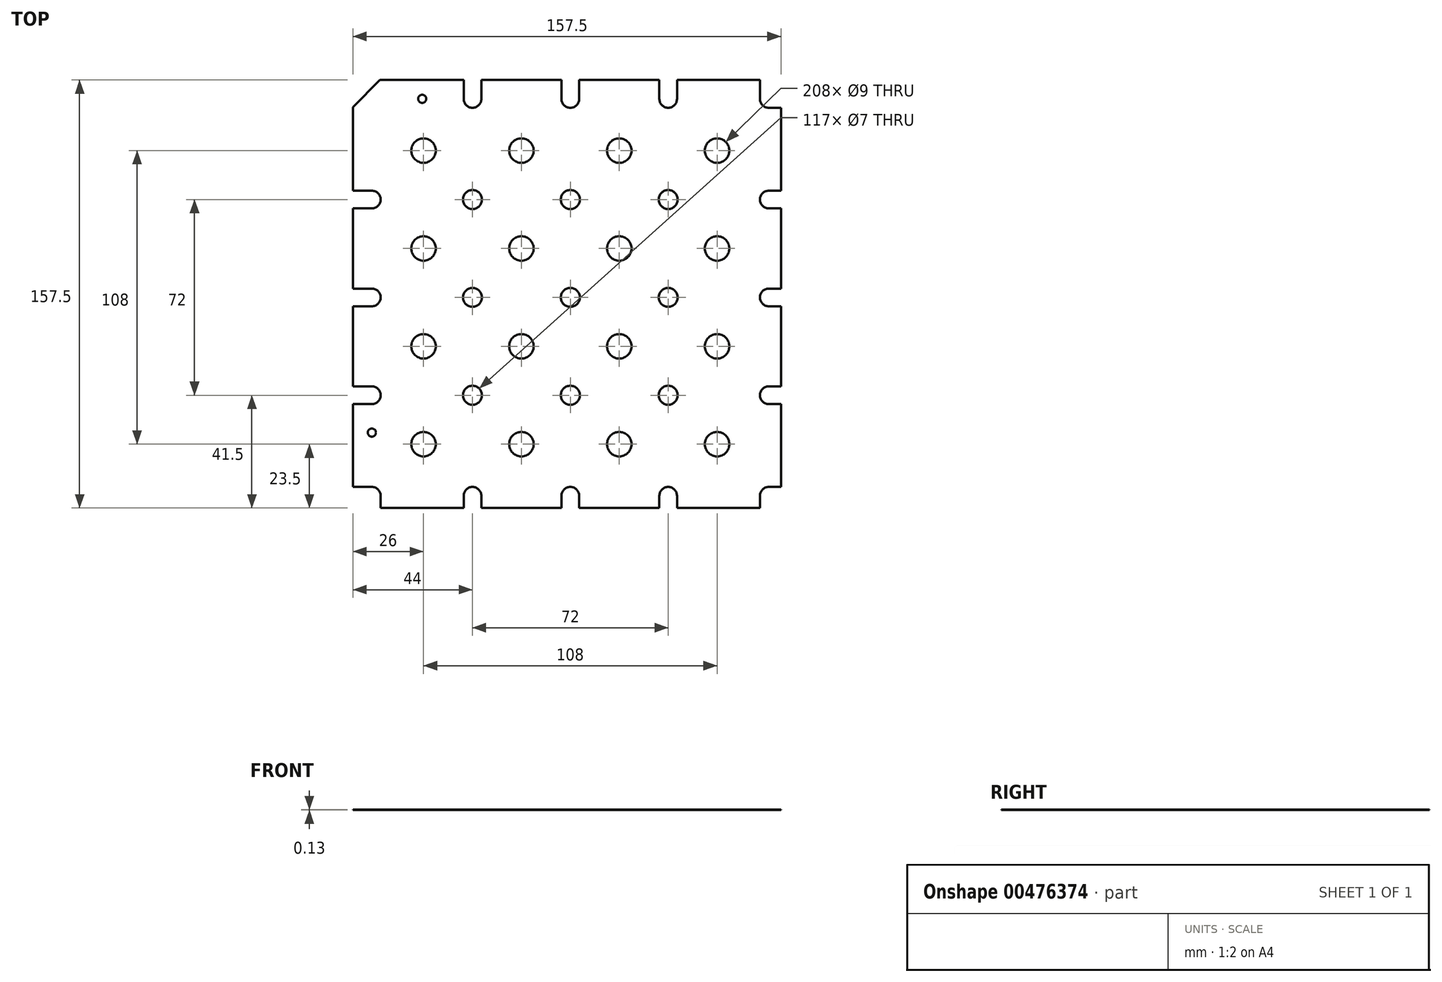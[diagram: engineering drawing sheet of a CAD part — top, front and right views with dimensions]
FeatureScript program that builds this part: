
annotation { "Feature Type Name" : "Feature", "Feature Type Description" : "" }
export const myFeature = defineFeature(function(context is Context, id is Id, definition is map)
    precondition{}
    {
        {
            var Q0;
            Q0=qCreatedBy(makeId("Top.planeOp"),FACE);
            var sketch = newSketch(context, id + "F0", { "sketchPlane" : qUnion([Q0])});
            skCircle(sketch, "E0", {"center": v(0, 0) * mm, "radius": 1.5 * mm});
            skCircle(sketch, "E1", {"center": v(18.5, 122.8) * mm, "radius": 1.5 * mm});
            skLineSegment(sketch, "E2.bottom", {"start": v(142.75, 129.75) * mm, "end": v(112.25, 129.75) * mm});
            skLineSegment(sketch, "E2.top", {"start": v(142.75, -27.75) * mm, "end": v(112.25, -27.75) * mm});
            skLineSegment(sketch, "E2.left", {"start": v(150.5, 119.5) * mm, "end": v(150.5, 89) * mm});
            skLineSegment(sketch, "E2.right", {"start": v(-7, 119.75) * mm, "end": v(-7, 89) * mm});
            skCircle(sketch, "E3", {"center": v(19, -4.25) * mm, "radius": 4.5 * mm});
            skCircle(sketch, "E4.0.1.0", {"center": v(19, 31.75) * mm, "radius": 4.5 * mm});
            skCircle(sketch, "E4.0.2.0", {"center": v(19, 67.75) * mm, "radius": 4.5 * mm});
            skCircle(sketch, "E4.0.3.0", {"center": v(19, 103.75) * mm, "radius": 4.5 * mm});
            skCircle(sketch, "E4.1.0.0", {"center": v(55, -4.25) * mm, "radius": 4.5 * mm});
            skCircle(sketch, "E4.1.1.0", {"center": v(55, 31.75) * mm, "radius": 4.5 * mm});
            skCircle(sketch, "E4.1.2.0", {"center": v(55, 67.75) * mm, "radius": 4.5 * mm});
            skCircle(sketch, "E4.1.3.0", {"center": v(55, 103.75) * mm, "radius": 4.5 * mm});
            skCircle(sketch, "E4.2.0.0", {"center": v(91, -4.25) * mm, "radius": 4.5 * mm});
            skCircle(sketch, "E4.2.1.0", {"center": v(91, 31.75) * mm, "radius": 4.5 * mm});
            skCircle(sketch, "E4.2.2.0", {"center": v(91, 67.75) * mm, "radius": 4.5 * mm});
            skCircle(sketch, "E4.2.3.0", {"center": v(91, 103.75) * mm, "radius": 4.5 * mm});
            skCircle(sketch, "E4.3.0.0", {"center": v(127, -4.25) * mm, "radius": 4.5 * mm});
            skCircle(sketch, "E4.3.1.0", {"center": v(127, 31.75) * mm, "radius": 4.5 * mm});
            skCircle(sketch, "E4.3.2.0", {"center": v(127, 67.75) * mm, "radius": 4.5 * mm});
            skCircle(sketch, "E4.3.3.0", {"center": v(127, 103.75) * mm, "radius": 4.5 * mm});
            skLineSegment(sketch, "E4.direction1", {"start": v(19, -4.25) * mm, "end": v(55, -4.25) * mm, "construction": true});
            skLineSegment(sketch, "E4.direction2", {"start": v(19, -4.25) * mm, "end": v(19, 31.75) * mm, "construction": true});
            skLineSegment(sketch, "E5", {"start": v(33.75, -23.25) * mm, "end": v(33.75, -27.75) * mm});
            skLineSegment(sketch, "E6", {"start": v(40.25, -23.25) * mm, "end": v(40.25, -27.75) * mm});
            skArc(sketch, "E7", {"start": v(33.75, -23.25) * mm, "mid": v(37, -20) * mm, "end": v(40.25, -23.25) * mm});
            skLineSegment(sketch, "E8.trimOffspring", {"start": v(33.75, -27.75) * mm, "end": v(3.25, -27.75) * mm});
            skLineSegment(sketch, "E9.1.0.0", {"start": v(69.75, -23.25) * mm, "end": v(69.75, -27.75) * mm});
            skArc(sketch, "E9.1.0.1", {"start": v(69.75, -23.25) * mm, "mid": v(73, -20) * mm, "end": v(76.25, -23.25) * mm});
            skLineSegment(sketch, "E9.1.0.2", {"start": v(76.25, -23.25) * mm, "end": v(76.25, -27.75) * mm});
            skLineSegment(sketch, "E9.2.0.0", {"start": v(105.75, -23.25) * mm, "end": v(105.75, -27.75) * mm});
            skArc(sketch, "E9.2.0.1", {"start": v(105.75, -23.25) * mm, "mid": v(109, -20) * mm, "end": v(112.25, -23.25) * mm});
            skLineSegment(sketch, "E9.2.0.2", {"start": v(112.25, -23.25) * mm, "end": v(112.25, -27.75) * mm});
            skLineSegment(sketch, "E9.direction1", {"start": v(40.25, -27.75) * mm, "end": v(69.75, -27.75) * mm, "construction": true});
            skLineSegment(sketch, "E10.trimOffspring", {"start": v(105.75, -27.75) * mm, "end": v(76.25, -27.75) * mm});
            skLineSegment(sketch, "E11.trimOffspring", {"start": v(69.75, -27.75) * mm, "end": v(40.25, -27.75) * mm});
            skLineSegment(sketch, "E12", {"start": v(0, -20) * mm, "end": v(-7, -20) * mm});
            skLineSegment(sketch, "E13", {"start": v(3.25, -23.25) * mm, "end": v(3.25, -27.75) * mm});
            skArc(sketch, "E14", {"start": v(3.25, -23.25) * mm, "mid": v(2.3, -20.95) * mm, "end": v(0, -20) * mm});
            skPoint(sketch, "E15.orphan", {"position": v(-7, -27.75) * mm});
            skLineSegment(sketch, "E16", {"start": v(142.75, -23.25) * mm, "end": v(142.75, -27.75) * mm});
            skLineSegment(sketch, "E17", {"start": v(146, -20) * mm, "end": v(150.5, -20) * mm});
            skPoint(sketch, "E17.startSnap0", {"position": v(37, -20) * mm});
            skArc(sketch, "E18", {"start": v(146, -20) * mm, "mid": v(143.7, -20.95) * mm, "end": v(142.75, -23.25) * mm});
            skLineSegment(sketch, "E19", {"start": v(146, 10.5) * mm, "end": v(150.5, 10.5) * mm});
            skLineSegment(sketch, "E20", {"start": v(146, 17) * mm, "end": v(150.5, 17) * mm});
            skArc(sketch, "E21", {"start": v(146, 17) * mm, "mid": v(142.75, 13.75) * mm, "end": v(146, 10.5) * mm});
            skLineSegment(sketch, "E22.0.1.0", {"start": v(146, 46.5) * mm, "end": v(150.5, 46.5) * mm});
            skArc(sketch, "E22.0.1.1", {"start": v(146, 53) * mm, "mid": v(142.75, 49.75) * mm, "end": v(146, 46.5) * mm});
            skLineSegment(sketch, "E22.0.1.2", {"start": v(146, 53) * mm, "end": v(150.5, 53) * mm});
            skLineSegment(sketch, "E22.0.2.0", {"start": v(146, 82.5) * mm, "end": v(150.5, 82.5) * mm});
            skArc(sketch, "E22.0.2.1", {"start": v(146, 89) * mm, "mid": v(142.75, 85.75) * mm, "end": v(146, 82.5) * mm});
            skLineSegment(sketch, "E22.0.2.2", {"start": v(146, 89) * mm, "end": v(150.5, 89) * mm});
            skLineSegment(sketch, "E23.trimOffspring", {"start": v(150.5, 46.5) * mm, "end": v(150.5, 17) * mm});
            skLineSegment(sketch, "E24.trimOffspring", {"start": v(150.5, 10.5) * mm, "end": v(150.5, -20) * mm});
            skLineSegment(sketch, "E25.trimOffspring", {"start": v(150.5, 82.5) * mm, "end": v(150.5, 53) * mm});
            skLineSegment(sketch, "E26", {"start": v(146, 119.5) * mm, "end": v(150.5, 119.5) * mm});
            skLineSegment(sketch, "E27", {"start": v(142.75, 122.75) * mm, "end": v(142.75, 129.75) * mm});
            skArc(sketch, "E28", {"start": v(146, 119.5) * mm, "mid": v(143.7, 120.45) * mm, "end": v(142.75, 122.75) * mm});
            skLineSegment(sketch, "E29", {"start": v(3, 129.75) * mm, "end": v(-7, 119.75) * mm});
            skPoint(sketch, "E30.orphan", {"position": v(-7, 129.75) * mm});
            skLineSegment(sketch, "E31", {"start": v(33.75, 129.75) * mm, "end": v(33.75, 122.75) * mm});
            skLineSegment(sketch, "E32", {"start": v(40.25, 129.75) * mm, "end": v(40.25, 122.75) * mm});
            skArc(sketch, "E33", {"start": v(33.75, 122.75) * mm, "mid": v(37, 119.5) * mm, "end": v(40.25, 122.75) * mm});
            skLineSegment(sketch, "E34.trimOffspring", {"start": v(33.75, 129.75) * mm, "end": v(3, 129.75) * mm});
            skArc(sketch, "E35.1.0.1", {"start": v(69.75, 122.75) * mm, "mid": v(73, 119.5) * mm, "end": v(76.25, 122.75) * mm});
            skArc(sketch, "E35.2.0.1", {"start": v(105.75, 122.75) * mm, "mid": v(109, 119.5) * mm, "end": v(112.25, 122.75) * mm});
            skLineSegment(sketch, "E35.direction1", {"start": v(33.75, 122.75) * mm, "end": v(37, 122.75) * mm, "construction": true});
            skLineSegment(sketch, "E36.trimOffspring", {"start": v(105.75, 129.75) * mm, "end": v(76.25, 129.75) * mm});
            skLineSegment(sketch, "E37.trimOffspring", {"start": v(69.75, 129.75) * mm, "end": v(40.25, 129.75) * mm});
            skLineSegment(sketch, "E38", {"start": v(-7, 10.5) * mm, "end": v(0, 10.5) * mm});
            skLineSegment(sketch, "E39", {"start": v(0, 17) * mm, "end": v(-7, 17) * mm});
            skLineSegment(sketch, "E40.0.1.0", {"start": v(-7, 46.5) * mm, "end": v(0, 46.5) * mm});
            skArc(sketch, "E40.0.1.1", {"start": v(0, 53) * mm, "mid": v(3.25, 49.75) * mm, "end": v(0, 46.5) * mm});
            skLineSegment(sketch, "E40.0.1.2", {"start": v(0, 53) * mm, "end": v(-7, 53) * mm});
            skLineSegment(sketch, "E40.0.2.0", {"start": v(-7, 82.5) * mm, "end": v(0, 82.5) * mm});
            skArc(sketch, "E40.0.2.1", {"start": v(0, 89) * mm, "mid": v(3.25, 85.75) * mm, "end": v(0, 82.5) * mm});
            skLineSegment(sketch, "E40.0.2.2", {"start": v(0, 89) * mm, "end": v(-7, 89) * mm});
            skLineSegment(sketch, "E40.direction1", {"start": v(-7, 10.5) * mm, "end": v(0, 10.5) * mm, "construction": true});
            skLineSegment(sketch, "E40.direction2", {"start": v(-7, 17) * mm, "end": v(-7, 46.5) * mm, "construction": true});
            skLineSegment(sketch, "E41.trimOffspring", {"start": v(-7, 46.5) * mm, "end": v(-7, 17) * mm});
            skLineSegment(sketch, "E42.trimOffspring", {"start": v(-7, 82.5) * mm, "end": v(-7, 53) * mm});
            skCircle(sketch, "E43", {"center": v(37, 13.75) * mm, "radius": 3.5 * mm});
            skCircle(sketch, "E44.0.1.0", {"center": v(37, 49.75) * mm, "radius": 3.5 * mm});
            skCircle(sketch, "E44.0.2.0", {"center": v(37, 85.75) * mm, "radius": 3.5 * mm});
            skCircle(sketch, "E44.1.0.0", {"center": v(73, 13.75) * mm, "radius": 3.5 * mm});
            skCircle(sketch, "E44.1.1.0", {"center": v(73, 49.75) * mm, "radius": 3.5 * mm});
            skCircle(sketch, "E44.1.2.0", {"center": v(73, 85.75) * mm, "radius": 3.5 * mm});
            skCircle(sketch, "E44.2.0.0", {"center": v(109, 13.75) * mm, "radius": 3.5 * mm});
            skCircle(sketch, "E44.2.1.0", {"center": v(109, 49.75) * mm, "radius": 3.5 * mm});
            skCircle(sketch, "E44.2.2.0", {"center": v(109, 85.75) * mm, "radius": 3.5 * mm});
            skLineSegment(sketch, "E44.direction1", {"start": v(37, 13.75) * mm, "end": v(73, 13.75) * mm, "construction": true});
            skLineSegment(sketch, "E44.direction2", {"start": v(37, 13.75) * mm, "end": v(37, 49.75) * mm, "construction": true});
            skLineSegment(sketch, "E45", {"start": v(69.75, 129.75) * mm, "end": v(69.75, 122.75) * mm});
            skLineSegment(sketch, "E46", {"start": v(76.25, 129.75) * mm, "end": v(76.25, 122.75) * mm});
            skLineSegment(sketch, "E47", {"start": v(105.75, 129.75) * mm, "end": v(105.75, 122.75) * mm});
            skLineSegment(sketch, "E48", {"start": v(112.25, 129.75) * mm, "end": v(112.25, 122.75) * mm});
            skArc(sketch, "E49", {"start": v(0, 10.5) * mm, "mid": v(3.25, 13.75) * mm, "end": v(0, 17) * mm});
            skLineSegment(sketch, "E50", {"start": v(-7, -20) * mm, "end": v(-7, 10.5) * mm});
            skSolve(sketch);
        }
        {
            var Q0;
            Q0=makeQuery(id+"F0.imprint","IMPRINT",FACE,{"disambiguationData":[TD([[makeQuery(id+"F0.imprint","IMPRINT",EDGE,{"derivedFrom":sQuery(id+"F0.wireOp",EDGE,"E0")}),-1.0]])]});
            extrude(context, id + "F1", {"entities" : qUnion([Q0]), "depth" : .125 * mm, "offsetDistance" : 25 * mm});
        }
    });
